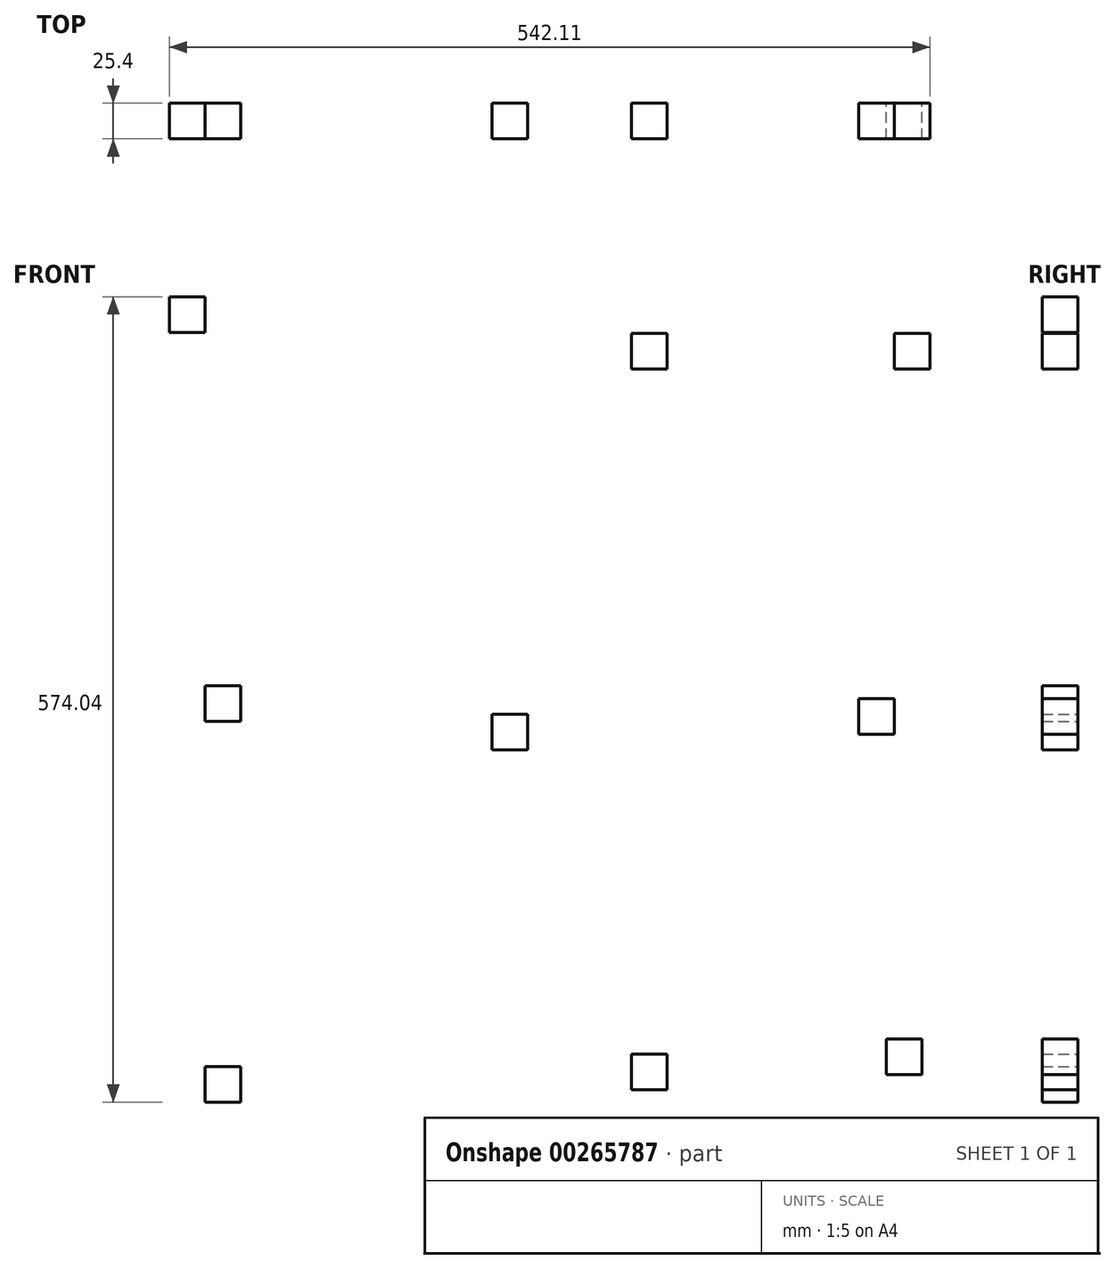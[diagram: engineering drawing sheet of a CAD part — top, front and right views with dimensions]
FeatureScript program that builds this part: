
annotation { "Feature Type Name" : "Feature", "Feature Type Description" : "" }
export const myFeature = defineFeature(function(context is Context, id is Id, definition is map)
    precondition{}
    {
        {
            var Q0;
            Q0=qCreatedBy(makeId("Front.planeOp"),FACE);
            var sketch = newSketch(context, id + "F0", { "sketchPlane" : qUnion([Q0])});
            skLineSegment(sketch, "E0.bottom", {"start": v(-292.34, 285.08) * mm, "end": v(-266.94, 285.08) * mm});
            skLineSegment(sketch, "E0.top", {"start": v(-292.34, 259.68) * mm, "end": v(-266.94, 259.68) * mm});
            skLineSegment(sketch, "E0.left", {"start": v(-292.34, 285.08) * mm, "end": v(-292.34, 259.68) * mm});
            skLineSegment(sketch, "E0.right", {"start": v(-266.94, 285.08) * mm, "end": v(-266.94, 259.68) * mm});
            skLineSegment(sketch, "E1.bottom", {"start": v(37.13, 258.96) * mm, "end": v(62.53, 258.96) * mm});
            skLineSegment(sketch, "E1.top", {"start": v(37.13, 233.56) * mm, "end": v(62.53, 233.56) * mm});
            skLineSegment(sketch, "E1.left", {"start": v(37.13, 258.96) * mm, "end": v(37.13, 233.56) * mm});
            skLineSegment(sketch, "E1.right", {"start": v(62.53, 258.96) * mm, "end": v(62.53, 233.56) * mm});
            skLineSegment(sketch, "E2.bottom", {"start": v(224.37, 258.96) * mm, "end": v(249.77, 258.96) * mm});
            skLineSegment(sketch, "E2.top", {"start": v(224.37, 233.56) * mm, "end": v(249.77, 233.56) * mm});
            skLineSegment(sketch, "E2.left", {"start": v(249.77, 258.96) * mm, "end": v(249.77, 233.56) * mm});
            skLineSegment(sketch, "E2.right", {"start": v(224.37, 258.96) * mm, "end": v(224.37, 233.56) * mm});
            skLineSegment(sketch, "E3.bottom", {"start": v(-266.94, 7.86) * mm, "end": v(-241.54, 7.86) * mm});
            skLineSegment(sketch, "E3.top", {"start": v(-266.94, -17.54) * mm, "end": v(-241.54, -17.54) * mm});
            skLineSegment(sketch, "E3.left", {"start": v(-266.94, 7.86) * mm, "end": v(-266.94, -17.54) * mm});
            skLineSegment(sketch, "E3.right", {"start": v(-241.54, 7.86) * mm, "end": v(-241.54, -17.54) * mm});
            skLineSegment(sketch, "E4.bottom", {"start": v(-62.29, -12.46) * mm, "end": v(-36.89, -12.46) * mm});
            skLineSegment(sketch, "E4.top", {"start": v(-62.29, -37.86) * mm, "end": v(-36.89, -37.86) * mm});
            skLineSegment(sketch, "E4.left", {"start": v(-62.29, -12.46) * mm, "end": v(-62.29, -37.86) * mm});
            skLineSegment(sketch, "E4.right", {"start": v(-36.89, -12.46) * mm, "end": v(-36.89, -37.86) * mm});
            skLineSegment(sketch, "E5.bottom", {"start": v(198.97, -1.57) * mm, "end": v(224.37, -1.57) * mm});
            skLineSegment(sketch, "E5.top", {"start": v(198.97, -26.97) * mm, "end": v(224.37, -26.97) * mm});
            skLineSegment(sketch, "E5.left", {"start": v(198.97, -1.57) * mm, "end": v(198.97, -26.97) * mm});
            skLineSegment(sketch, "E5.right", {"start": v(224.37, -1.57) * mm, "end": v(224.37, -26.97) * mm});
            skLineSegment(sketch, "E6.bottom", {"start": v(-266.94, -263.56) * mm, "end": v(-241.54, -263.56) * mm});
            skLineSegment(sketch, "E6.top", {"start": v(-266.94, -288.96) * mm, "end": v(-241.54, -288.96) * mm});
            skLineSegment(sketch, "E6.left", {"start": v(-266.94, -263.56) * mm, "end": v(-266.94, -288.96) * mm});
            skLineSegment(sketch, "E6.right", {"start": v(-241.54, -263.56) * mm, "end": v(-241.54, -288.96) * mm});
            skLineSegment(sketch, "E7.bottom", {"start": v(37.13, -254.85) * mm, "end": v(62.53, -254.85) * mm});
            skLineSegment(sketch, "E7.top", {"start": v(37.13, -280.25) * mm, "end": v(62.53, -280.25) * mm});
            skLineSegment(sketch, "E7.left", {"start": v(37.13, -254.85) * mm, "end": v(37.13, -280.25) * mm});
            skLineSegment(sketch, "E7.right", {"start": v(62.53, -254.85) * mm, "end": v(62.53, -280.25) * mm});
            skLineSegment(sketch, "E8.bottom", {"start": v(218.56, -243.96) * mm, "end": v(243.96, -243.96) * mm});
            skLineSegment(sketch, "E8.top", {"start": v(218.56, -269.36) * mm, "end": v(243.96, -269.36) * mm});
            skLineSegment(sketch, "E8.left", {"start": v(218.56, -243.96) * mm, "end": v(218.56, -269.36) * mm});
            skLineSegment(sketch, "E8.right", {"start": v(243.96, -243.96) * mm, "end": v(243.96, -269.36) * mm});
            skSolve(sketch);
        }
        {
            var Q0;
            Q0 = qSketchRegion(id + "F0", true);
            extrude(context, id + "F1", {"entities" : qUnion([Q0]), "depth" : 25.4 * mm});
        }
    });
